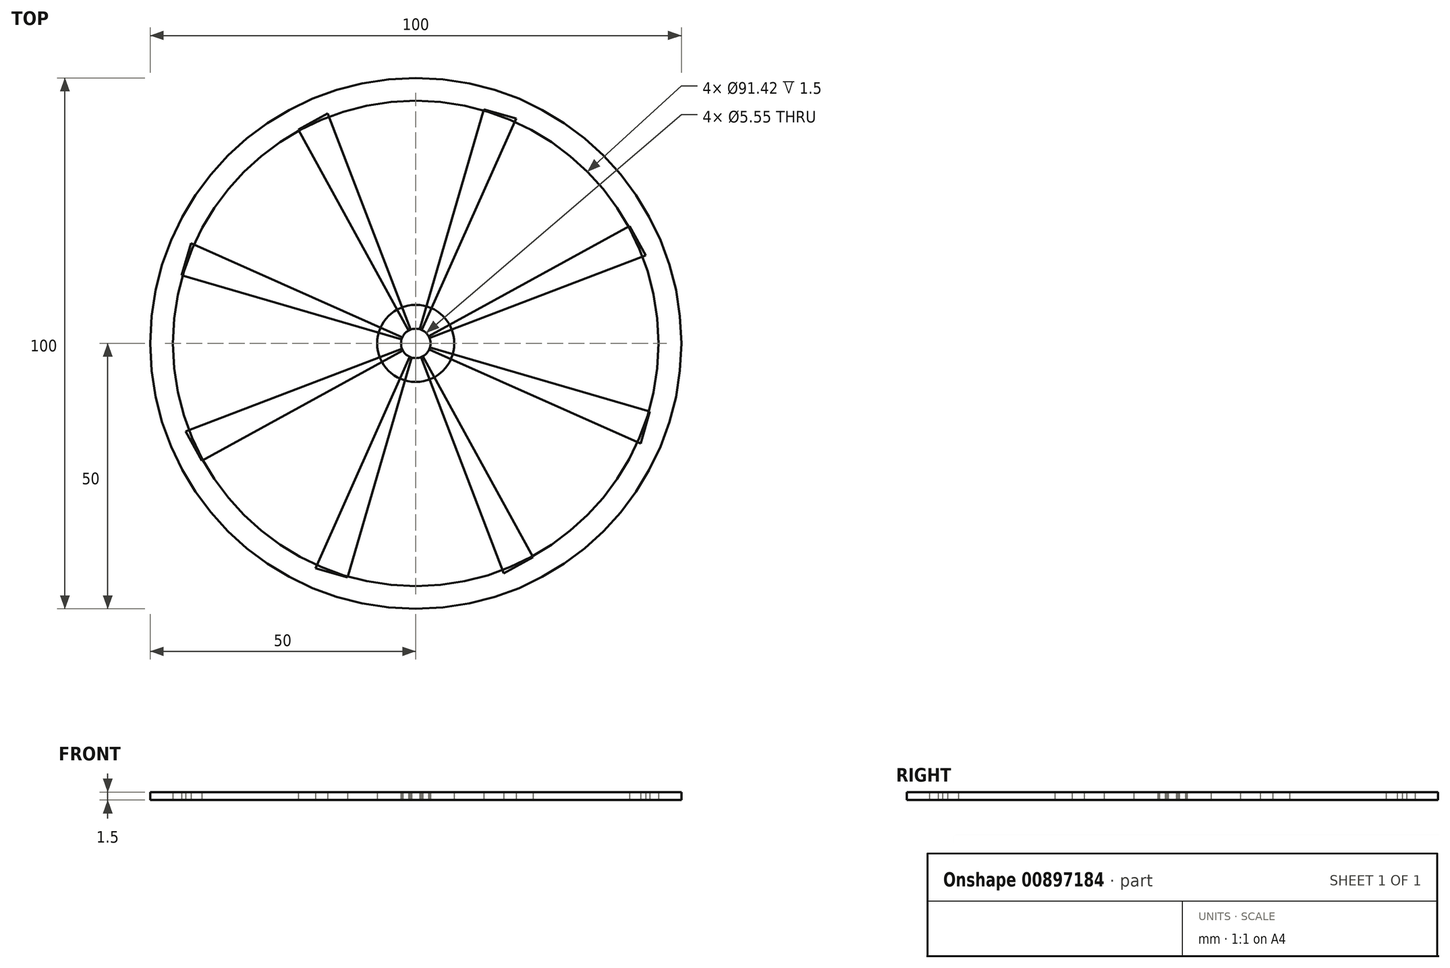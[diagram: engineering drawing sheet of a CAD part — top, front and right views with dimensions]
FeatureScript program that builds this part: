
annotation { "Feature Type Name" : "Feature", "Feature Type Description" : "" }
export const myFeature = defineFeature(function(context is Context, id is Id, definition is map)
    precondition{}
    {
        {
            var Q0;
            Q0=qCreatedBy(makeId("Top.planeOp"),FACE);
            var sketch = newSketch(context, id + "F0", { "sketchPlane" : qUnion([Q0])});
            skCircle(sketch, "E0", {"center": v(0, 0) * mm, "radius": 50 * mm});
            skSolve(sketch);
        }
        {
            var Q0;
            Q0=makeQuery(id+"F0.imprint","IMPRINT",FACE,{"disambiguationData":[TD([[makeQuery(id+"F0.imprint","IMPRINT",EDGE,{"derivedFrom":sQuery(id+"F0.wireOp",EDGE,"E0")}),1.0]])]});
            var sketch = newSketch(context, id + "F1", { "sketchPlane" : qUnion([Q0])});
            skCircle(sketch, "E1", {"center": v(0, 0) * mm, "radius": 45.71 * mm});
            skSolve(sketch);
        }
        {
            var Q0;
            Q0=makeQuery(id+"F1.imprint","IMPRINT",FACE,{"disambiguationData":[TD([[makeQuery(id+"F1.imprint","IMPRINT",EDGE,{"derivedFrom":sQuery(id+"F1.wireOp",EDGE,"E1")}),-1.0]])]});
            var Q1;
            Q1=sQuery(id+"F0.wireOp",EDGE,"E0");
            extrude(context, id + "F2", {"entities" : qUnion([Q0]), "surfaceEntities" : qUnion([Q1]), "depth" : 1.5 * mm, "offsetDistance" : 25 * mm});
        }
        {
            var Q0;
            Q0=qCreatedBy(makeId("Top.planeOp"),FACE);
            var sketch = newSketch(context, id + "F3", { "sketchPlane" : qUnion([Q0])});
            skCircle(sketch, "E2", {"center": v(0, 0) * mm, "radius": 7.26 * mm});
            skSolve(sketch);
        }
        {
            var Q0;
            Q0=makeQuery(id+"F3.imprint","IMPRINT",FACE,{"disambiguationData":[TD([[makeQuery(id+"F3.imprint","IMPRINT",EDGE,{"derivedFrom":sQuery(id+"F3.wireOp",EDGE,"E2")}),1.0]])]});
            extrude(context, id + "F4", {"entities" : qUnion([Q0]), "depth" : 1.5 * mm, "offsetDistance" : 25 * mm});
        }
        {
            var Q0;
            Q0=qCreatedBy(makeId("Top.planeOp"),FACE);
            var sketch = newSketch(context, id + "F5", { "sketchPlane" : qUnion([Q0])});
            skLineSegment(sketch, "E3", {"start": v(0, 0) * mm, "end": v(-22.1, 40.25) * mm});
            skLineSegment(sketch, "E4", {"start": v(-22.1, 40.25) * mm, "end": v(-16.57, 43.29) * mm});
            skLineSegment(sketch, "E5", {"start": v(-16.57, 43.29) * mm, "end": v(0, 0) * mm});
            skSolve(sketch);
        }
        {
            var Q0;
            Q0=makeQuery(id+"F5.imprint","IMPRINT",FACE,{"disambiguationData":[TD([[makeQuery(id+"F5.imprint","IMPRINT",EDGE,{"derivedFrom":sQuery(id+"F5.wireOp",EDGE,"E3")}),-1.0]])]});
            extrude(context, id + "F6", {"entities" : qUnion([Q0]), "depth" : 1.5 * mm, "offsetDistance" : 25 * mm});
        }
        {
            var Q0;
            Q0=makeQuery(id+"F6.opExtrude","SWEPT_BODY",BODY,{"disambiguationData":[OSD([sQuery(id+"F5.wireOp",EDGE,"E3"),sQuery(id+"F5.wireOp",EDGE,"E4"),sQuery(id+"F5.wireOp",EDGE,"E5")])]});
            var Q1;
            Q1=makeQuery(id+"F4.opExtrude","CAP_EDGE",EDGE,{"disambiguationData":[OSD([sQuery(id+"F3.wireOp",EDGE,"E2")])],"isStart":false});
            circularPattern(context, id + "F7", {"entities" : qUnion([Q0]), "axis" : qUnion([Q1]), "angle" : 360 * degree, "instanceCount" : 8, "equalSpace" : true});
        }
        {
            var Q0;
            Q0=qCreatedBy(makeId("Top.planeOp"),FACE);
            var sketch = newSketch(context, id + "F8", { "sketchPlane" : qUnion([Q0])});
            skCircle(sketch, "E6", {"center": v(0, 0) * mm, "radius": 2.78 * mm});
            skSolve(sketch);
        }
        {
            var Q0;
            Q0=makeQuery(id+"F8.imprint","IMPRINT",FACE,{"disambiguationData":[TD([[makeQuery(id+"F8.imprint","IMPRINT",EDGE,{"derivedFrom":sQuery(id+"F8.wireOp",EDGE,"E6")}),1.0]])]});
            var Q1;
            Q1=sQuery(id+"F8.wireOp",EDGE,"E6");
            extrude(context, id + "F9", {"entities" : qUnion([Q0]), "operationType" : NewBodyOperationType.REMOVE, "surfaceEntities" : qUnion([Q1]), "depth" : 1.5 * mm, "offsetDistance" : 25 * mm});
        }
    });
